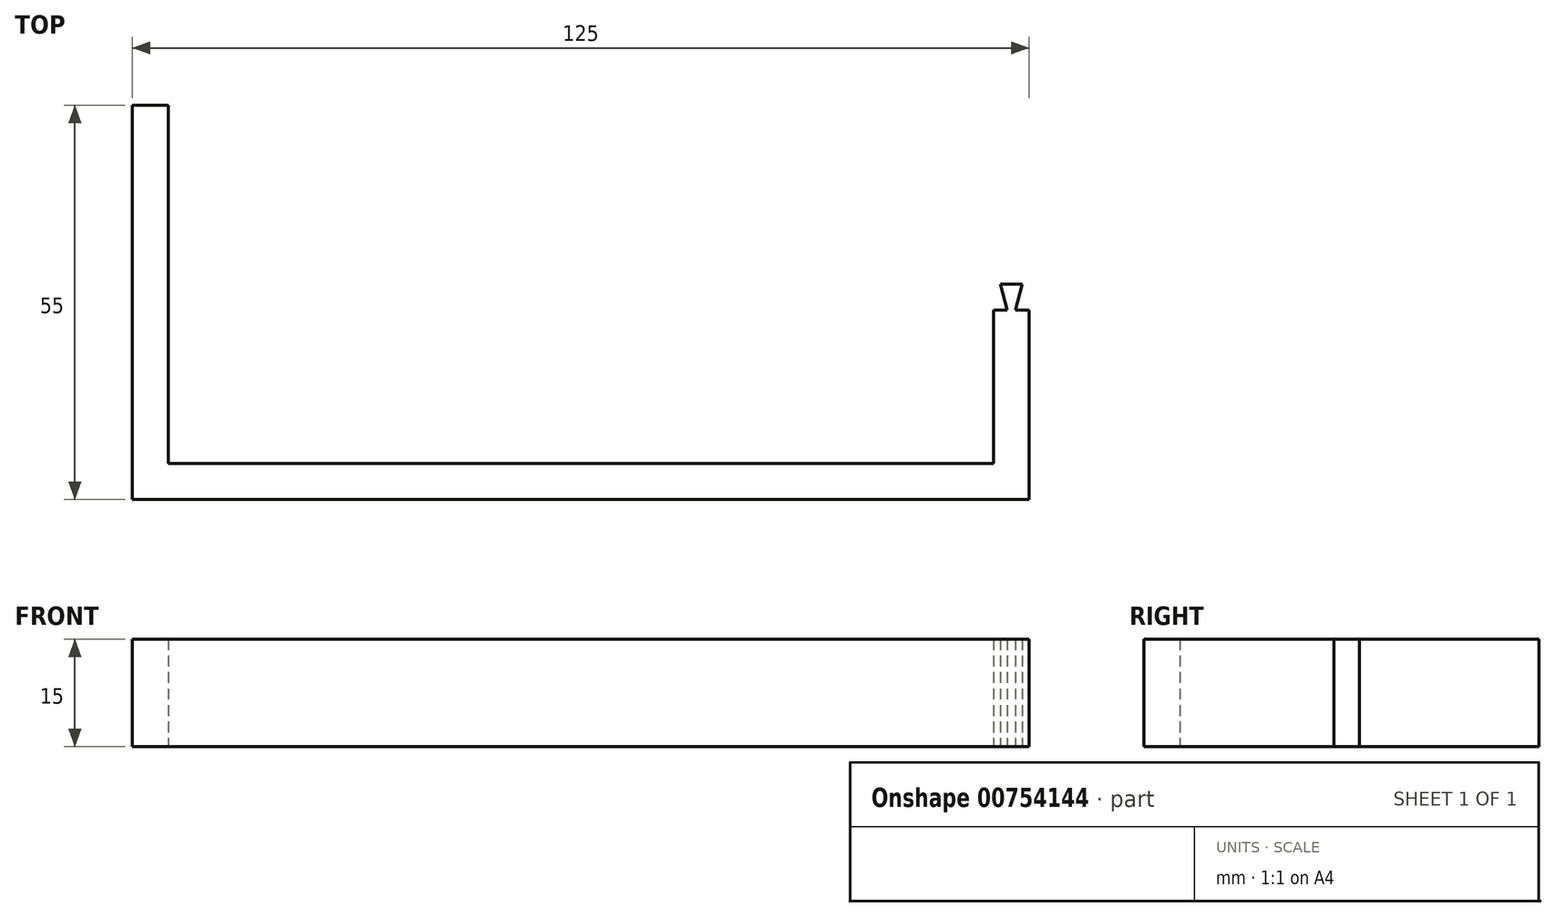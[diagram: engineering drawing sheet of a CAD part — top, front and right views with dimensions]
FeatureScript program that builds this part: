
annotation { "Feature Type Name" : "Feature", "Feature Type Description" : "" }
export const myFeature = defineFeature(function(context is Context, id is Id, definition is map)
    precondition{}
    {
        {
            var Q0;
            Q0=qCreatedBy(makeId("Top.planeOp"),FACE);
            var sketch = newSketch(context, id + "F0", { "sketchPlane" : qUnion([Q0])});
            skLineSegment(sketch, "E0", {"start": v(-171.38, 166.5) * mm, "end": v(-171.38, 111.5) * mm});
            skLineSegment(sketch, "E1", {"start": v(-171.38, 111.5) * mm, "end": v(-46.38, 111.5) * mm});
            skLineSegment(sketch, "E2", {"start": v(-46.38, 111.5) * mm, "end": v(-46.38, 141.5) * mm});
            skLineSegment(sketch, "E3", {"start": v(-171.38, 166.5) * mm, "end": v(-166.38, 166.5) * mm});
            skLineSegment(sketch, "E4", {"start": v(-166.38, 166.5) * mm, "end": v(-166.38, 116.5) * mm});
            skLineSegment(sketch, "E5", {"start": v(-166.38, 116.5) * mm, "end": v(-51.38, 116.5) * mm});
            skLineSegment(sketch, "E6", {"start": v(-51.38, 116.5) * mm, "end": v(-51.38, 141.5) * mm});
            skLineSegment(sketch, "E7", {"start": v(-51.38, 141.5) * mm, "end": v(-46.38, 141.5) * mm});
            skLineSegment(sketch, "E8", {"start": v(-51.38, 137.94) * mm, "end": v(-46.38, 137.94) * mm});
            skLineSegment(sketch, "E9", {"start": v(-50.38, 141.5) * mm, "end": v(-49.43, 137.94) * mm});
            skLineSegment(sketch, "E10", {"start": v(-47.38, 141.5) * mm, "end": v(-48.33, 137.94) * mm});
            skLineSegment(sketch, "E11", {"start": v(-48.88, 141.5) * mm, "end": v(-48.88, 137.94) * mm, "construction": true});
            skSolve(sketch);
        }
        {
            var Q0;
            Q0=makeQuery(id+"F0.imprint","IMPRINT",FACE,{"disambiguationData":[TD([[makeQuery(id+"F0.imprint","IMPRINT",EDGE,{"derivedFrom":sQuery(id+"F0.wireOp",EDGE,"E0")}),1.0]])]});
            var Q1;
            {var subQ0=sQuery(id+"F0.wireOp",EDGE,"E9");Q1=makeQuery(id+"F0.imprint","IMPRINT",FACE,{"disambiguationData":[TD([[makeQuery(id+"F0.imprint","IMPRINT",EDGE,{"derivedFrom":subQ0}),1.0]])]});}
            extrude(context, id + "F1", {"entities" : qUnion([Q0, Q1]), "depth" : 15 * mm, "offsetDistance" : 25 * mm});
        }
    });
